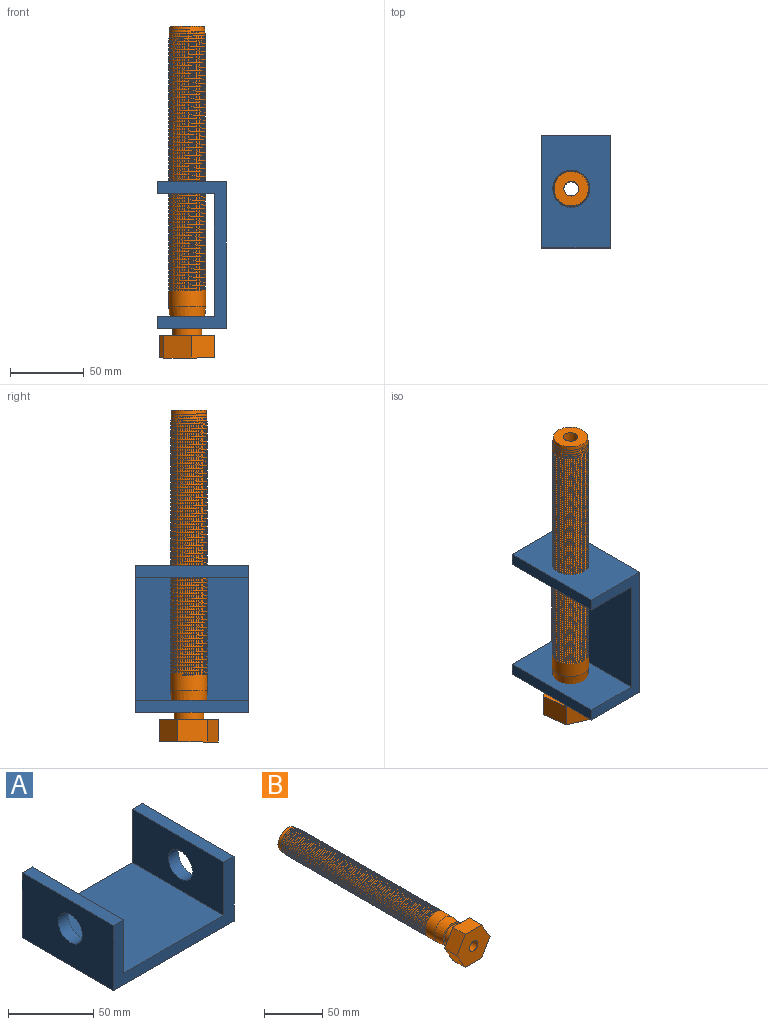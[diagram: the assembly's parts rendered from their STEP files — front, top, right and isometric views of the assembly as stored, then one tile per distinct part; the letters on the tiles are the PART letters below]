
ASSEMBLY  parts=2 mates=1
PART A: 12 faces, bbox 99.5x76x46.5 mm
  f0: plane 82.91x76mm, normal (0,0,1), area 6301.2mm2, adj f1,f7,f8,f9
  f1: plane 76x38.19mm, normal (1,0,0), area 2588mm2, adj f0,f2,f8,f9,f11
  f2: plane 76x8.3mm, normal (0,0,1), area 630.8mm2, adj f1,f3,f8,f9
  f3: plane 76x46.49mm, normal (-1,0,0), area 3218.8mm2, adj f2,f4,f8,f9,f11
  f4: plane 99.51x76mm, normal (0,0,-1), area 7562.8mm2, adj f3,f5,f8,f9
  f5: plane 76x46.49mm, normal (1,0,0), area 3218.8mm2, adj f4,f6,f8,f9,f10
  f6: plane 76x8.3mm, normal (0,0,1), area 630.8mm2, adj f5,f7,f8,f9
  f7: plane 76x38.19mm, normal (-1,0,0), area 2588mm2, adj f0,f6,f8,f9,f10
  f8: plane 99.51x46.49mm, normal (0,-1,0), area 1459.8mm2, adj f0,f1,f2,f3,f4,f5,f6,f7
  f9: plane 99.51x46.49mm, normal (0,1,0), area 1459.8mm2, adj f0,f1,f2,f3,f4,f5,f6,f7
  f10: cylinder r=10mm len=20mm, axis (1,0,0), area 521.5mm2, adj f5,f7
  f11: cylinder r=10mm len=20mm, axis (1,0,0), area 521.5mm2, adj f1,f3
PART B: 116 faces, bbox 40x225x34.6 mm
  f0: cylinder r=12.5mm len=25mm, axis (0,-1,0), area 899.1mm2, adj f93,f111,f112,f113,f114
  f1: cylinder r=12.5mm len=25mm, axis (0,-1,0), area 77.3mm2, adj f2,f94,f113,f114
  f2: cylinder r=12.5mm len=25mm, axis (0,-1,0), area 77.3mm2, adj f1,f3,f113,f114
  f3: cylinder r=12.5mm len=25mm, axis (0,-1,0), area 77.2mm2, adj f2,f4,f113,f114
  f4: cylinder r=12.5mm len=25mm, axis (0,-1,0), area 77.3mm2, adj f3,f5,f113,f114
  f5: cylinder r=12.5mm len=25mm, axis (0,-1,0), area 77.3mm2, adj f4,f6,f113,f114
  f6: cylinder r=12.5mm len=25mm, axis (0,-1,0), area 77.3mm2, adj f5,f7,f113,f114
  f7: cylinder r=12.5mm len=25mm, axis (0,-1,0), area 77.3mm2, adj f6,f8,f113,f114
  f8: cylinder r=12.5mm len=25mm, axis (0,-1,0), area 77.3mm2, adj f7,f9,f113,f114
  f9: cylinder r=12.5mm len=25mm, axis (0,-1,0), area 77.3mm2, adj f8,f10,f113,f114
  f10: cylinder r=12.5mm len=25mm, axis (0,-1,0), area 77.4mm2, adj f9,f11,f113,f114
  f11: cylinder r=12.5mm len=25mm, axis (0,-1,0), area 77.4mm2, adj f10,f12,f113,f114
  f12: cylinder r=12.5mm len=25mm, axis (0,-1,0), area 77.3mm2, adj f11,f13,f113,f114
  f13: cylinder r=12.5mm len=25mm, axis (0,-1,0), area 77.3mm2, adj f12,f14,f113,f114
  f14: cylinder r=12.5mm len=25mm, axis (0,-1,0), area 77.3mm2, adj f13,f15,f113,f114
  f15: cylinder r=12.5mm len=25mm, axis (0,-1,0), area 77.4mm2, adj f14,f16,f113,f114
  f16: cylinder r=12.5mm len=25mm, axis (0,-1,0), area 77.3mm2, adj f15,f17,f113,f114
  f17: cylinder r=12.5mm len=25mm, axis (0,-1,0), area 77.3mm2, adj f16,f18,f113,f114
  f18: cylinder r=12.5mm len=25mm, axis (0,-1,0), area 77.3mm2, adj f17,f19,f113,f114
  f19: cylinder r=12.5mm len=25mm, axis (0,-1,0), area 77.3mm2, adj f18,f20,f113,f114
  f20: cylinder r=12.5mm len=25mm, axis (0,-1,0), area 77.3mm2, adj f19,f21,f113,f114
  f21: cylinder r=12.5mm len=25mm, axis (0,-1,0), area 77.3mm2, adj f20,f22,f113,f114
  f22: cylinder r=12.5mm len=25mm, axis (0,-1,0), area 77.3mm2, adj f21,f23,f113,f114
  f23: cylinder r=12.5mm len=25mm, axis (0,-1,0), area 77.2mm2, adj f22,f24,f113,f114
  f24: cylinder r=12.5mm len=25mm, axis (0,-1,0), area 77.3mm2, adj f23,f25,f113,f114
  f25: cylinder r=12.5mm len=25mm, axis (0,-1,0), area 77.3mm2, adj f24,f26,f113,f114
  f26: cylinder r=12.5mm len=25mm, axis (0,-1,0), area 77.3mm2, adj f25,f27,f113,f114
  f27: cylinder r=12.5mm len=25mm, axis (0,-1,0), area 77.3mm2, adj f26,f28,f113,f114
  f28: cylinder r=12.5mm len=25mm, axis (0,-1,0), area 77.3mm2, adj f27,f29,f113,f114
  f29: cylinder r=12.5mm len=25mm, axis (0,-1,0), area 77.3mm2, adj f28,f30,f113,f114
  f30: cylinder r=12.5mm len=25mm, axis (0,-1,0), area 77.3mm2, adj f29,f31,f113,f114
  f31: cylinder r=12.5mm len=25mm, axis (0,-1,0), area 77.4mm2, adj f30,f32,f113,f114
  f32: cylinder r=12.5mm len=25mm, axis (0,-1,0), area 77.3mm2, adj f31,f33,f113,f114
  f33: cylinder r=12.5mm len=25mm, axis (0,-1,0), area 77.3mm2, adj f32,f34,f113,f114
  f34: cylinder r=12.5mm len=25mm, axis (0,-1,0), area 77.3mm2, adj f33,f35,f113,f114
  f35: cylinder r=12.5mm len=25mm, axis (0,-1,0), area 77.3mm2, adj f34,f36,f113,f114
  f36: cylinder r=12.5mm len=25mm, axis (0,-1,0), area 77.4mm2, adj f35,f37,f113,f114
  f37: cylinder r=12.5mm len=25mm, axis (0,-1,0), area 77.3mm2, adj f36,f38,f113,f114
  f38: cylinder r=12.5mm len=25mm, axis (0,-1,0), area 77.3mm2, adj f37,f39,f113,f114
  f39: cylinder r=12.5mm len=25mm, axis (0,-1,0), area 77.3mm2, adj f38,f40,f113,f114
  f40: cylinder r=12.5mm len=25mm, axis (0,-1,0), area 77.3mm2, adj f39,f41,f113,f114
  f41: cylinder r=12.5mm len=25mm, axis (0,-1,0), area 77.3mm2, adj f40,f42,f113,f114
  f42: cylinder r=12.5mm len=25mm, axis (0,-1,0), area 77.3mm2, adj f41,f43,f113,f114
  f43: cylinder r=12.5mm len=25mm, axis (0,-1,0), area 77.3mm2, adj f42,f44,f113,f114
  f44: cylinder r=12.5mm len=25mm, axis (0,-1,0), area 77.2mm2, adj f43,f45,f113,f114
  f45: cylinder r=12.5mm len=25mm, axis (0,-1,0), area 77.3mm2, adj f44,f46,f113,f114
  f46: cylinder r=12.5mm len=25mm, axis (0,-1,0), area 77.3mm2, adj f45,f47,f113,f114
  f47: cylinder r=12.5mm len=25mm, axis (0,-1,0), area 77.3mm2, adj f46,f48,f113,f114
  f48: cylinder r=12.5mm len=25mm, axis (0,-1,0), area 77.3mm2, adj f47,f49,f113,f114
  f49: cylinder r=12.5mm len=25mm, axis (0,-1,0), area 77.3mm2, adj f48,f50,f113,f114
  f50: cylinder r=12.5mm len=25mm, axis (0,-1,0), area 77.3mm2, adj f49,f51,f113,f114
  f51: cylinder r=12.5mm len=25mm, axis (0,-1,0), area 77.4mm2, adj f50,f52,f113,f114
  f52: cylinder r=12.5mm len=25mm, axis (0,-1,0), area 77.4mm2, adj f51,f53,f113,f114
  f53: cylinder r=12.5mm len=25mm, axis (0,-1,0), area 77.3mm2, adj f52,f54,f113,f114
  f54: cylinder r=12.5mm len=25mm, axis (0,-1,0), area 77.3mm2, adj f53,f55,f113,f114
  f55: cylinder r=12.5mm len=25mm, axis (0,-1,0), area 77.3mm2, adj f54,f56,f113,f114
  f56: cylinder r=12.5mm len=25mm, axis (0,-1,0), area 77.4mm2, adj f55,f57,f113,f114
  f57: cylinder r=12.5mm len=25mm, axis (0,-1,0), area 77.3mm2, adj f56,f58,f113,f114
  f58: cylinder r=12.5mm len=25mm, axis (0,-1,0), area 77.3mm2, adj f57,f59,f113,f114
  f59: cylinder r=12.5mm len=25mm, axis (0,-1,0), area 77.3mm2, adj f58,f60,f113,f114
  f60: cylinder r=12.5mm len=25mm, axis (0,-1,0), area 77.3mm2, adj f59,f61,f113,f114
  f61: cylinder r=12.5mm len=25mm, axis (0,-1,0), area 77.3mm2, adj f60,f62,f113,f114
  f62: cylinder r=12.5mm len=25mm, axis (0,-1,0), area 77.3mm2, adj f61,f63,f113,f114
  f63: cylinder r=12.5mm len=25mm, axis (0,-1,0), area 77.3mm2, adj f62,f64,f113,f114
  f64: cylinder r=12.5mm len=25mm, axis (0,-1,0), area 77.2mm2, adj f63,f65,f113,f114
  f65: cylinder r=12.5mm len=25mm, axis (0,-1,0), area 77.3mm2, adj f64,f66,f113,f114
  f66: cylinder r=12.5mm len=25mm, axis (0,-1,0), area 77.3mm2, adj f65,f67,f113,f114
  f67: cylinder r=12.5mm len=25mm, axis (0,-1,0), area 77.3mm2, adj f66,f68,f113,f114
  f68: cylinder r=12.5mm len=25mm, axis (0,-1,0), area 77.3mm2, adj f67,f69,f113,f114
  f69: cylinder r=12.5mm len=25mm, axis (0,-1,0), area 77.3mm2, adj f68,f70,f113,f114
  f70: cylinder r=12.5mm len=25mm, axis (0,-1,0), area 77.3mm2, adj f69,f71,f113,f114
  f71: cylinder r=12.5mm len=25mm, axis (0,-1,0), area 77.3mm2, adj f70,f72,f113,f114
  f72: cylinder r=12.5mm len=25mm, axis (0,-1,0), area 77.4mm2, adj f71,f73,f113,f114
  f73: cylinder r=12.5mm len=25mm, axis (0,-1,0), area 77.3mm2, adj f72,f74,f113,f114
  f74: cylinder r=12.5mm len=25mm, axis (0,-1,0), area 77.3mm2, adj f73,f75,f113,f114
  f75: cylinder r=12.5mm len=25mm, axis (0,-1,0), area 77.3mm2, adj f74,f76,f113,f114
  f76: cylinder r=12.5mm len=25mm, axis (0,-1,0), area 77.4mm2, adj f75,f77,f113,f114
  f77: cylinder r=12.5mm len=25mm, axis (0,-1,0), area 77.4mm2, adj f76,f78,f113,f114
  f78: cylinder r=12.5mm len=25mm, axis (0,-1,0), area 77.3mm2, adj f77,f79,f113,f114
  f79: cylinder r=12.5mm len=25mm, axis (0,-1,0), area 77.3mm2, adj f78,f80,f113,f114
  f80: cylinder r=12.5mm len=25mm, axis (0,-1,0), area 77.3mm2, adj f79,f81,f113,f114
  f81: cylinder r=12.5mm len=25mm, axis (0,-1,0), area 77.3mm2, adj f80,f82,f113,f114
  f82: cylinder r=12.5mm len=25mm, axis (0,-1,0), area 77.3mm2, adj f81,f83,f113,f114
  f83: cylinder r=12.5mm len=25mm, axis (0,-1,0), area 77.3mm2, adj f82,f84,f113,f114
  f84: cylinder r=12.5mm len=25mm, axis (0,-1,0), area 77.2mm2, adj f83,f85,f113,f114
  f85: cylinder r=12.5mm len=25mm, axis (0,-1,0), area 77.2mm2, adj f84,f86,f113,f114
  f86: cylinder r=12.5mm len=25mm, axis (0,-1,0), area 77.3mm2, adj f85,f87,f113,f114
  f87: cylinder r=12.5mm len=25mm, axis (0,-1,0), area 77.3mm2, adj f86,f88,f113,f114
  f88: cylinder r=12.5mm len=25mm, axis (0,-1,0), area 77.3mm2, adj f87,f89,f113,f114
  f89: cylinder r=12.5mm len=25mm, axis (0,-1,0), area 77.3mm2, adj f88,f90,f113,f114
  f90: cylinder r=12.5mm len=25mm, axis (0,-1,0), area 77.3mm2, adj f89,f91,f113,f114
  f91: cylinder r=12.5mm len=25mm, axis (0,-1,0), area 77.3mm2, adj f90,f92,f113,f114
  f92: cylinder r=12.5mm len=25mm, axis (0,-1,0), area 77.4mm2, adj f91,f93,f113,f114
  f93: cylinder r=12.5mm len=25mm, axis (0,-1,0), area 77.4mm2, adj f0,f92,f113,f114
  f94: cylinder r=12.5mm len=24.17mm, axis (0,-1,0), area 21.2mm2, adj f1,f110,f113
  f95: plane 20x15mm, normal (0,0,1), area 300mm2, adj f96,f100,f101,f102
  f96: plane 17.32x15mm, normal (-0.87,0,0.5), area 300mm2, adj f95,f97,f101,f102
  f97: plane 17.32x15mm, normal (-0.87,0,-0.5), area 300mm2, adj f96,f98,f101,f102
  f98: plane 20x15mm, normal (0,0,-1), area 300mm2, adj f97,f99,f101,f102
  f99: plane 17.32x15mm, normal (0.87,0,-0.5), area 300mm2, adj f98,f100,f101,f102
  f100: plane 17.32x15mm, normal (0.87,0,0.5), area 300mm2, adj f95,f99,f101,f102
  f101: plane 40x34.64mm, normal (0,-1,0), area 960.7mm2, adj f95,f96,f97,f98,f99,f100,f115
  f102: plane 40x34.64mm, normal (0,1,0), area 725.1mm2, adj f95,f96,f97,f98,f99,f100,f103
  f103: cylinder r=10mm len=20mm, axis (0,-1,0), area 628.3mm2, adj f102,f105
  f104: plane 23.25x23.25mm, normal (0,1,0), area 346mm2, adj f106,f115
  f105: plane 23.25x23.25mm, normal (0,-1,0), area 110.4mm2, adj f103,f111
  f106: cone r=11.63mm half-angle=5deg, axis (0,-1,0), area 241.2mm2, adj f104,f107,f113,f114
  f107: cone r=11.63mm half-angle=5deg, axis (0,-1,0), area 121.5mm2, adj f106,f108,f113,f114
  f108: cone r=11.63mm half-angle=5deg, axis (0,-1,0), area 108.4mm2, adj f107,f109,f113,f114
  f109: cone r=11.63mm half-angle=5deg, axis (0,-1,0), area 94.8mm2, adj f108,f110,f113,f114
  f110: cone r=11.63mm half-angle=5deg, axis (0,-1,0), area 60.9mm2, adj f94,f109,f113,f114
  f111: cone r=12.5mm half-angle=5deg, axis (0,1,0), area 760.8mm2, adj f0,f105
  f112: plane 0.82x0.67mm, normal (0,0,-1), area 0.3mm2, adj f0,f113,f114
  f113: bspline ~177.6x29.55mm, area 5738.9mm2, adj f0,f1,f2,f3,f4,f5,f6,f7
  f114: bspline ~177.63x29.75mm, area 5748.1mm2, adj f0,f1,f2,f3,f4,f5,f6,f7
  f115: cylinder r=5mm len=225mm, axis (0,-1,0), area 7068.6mm2, adj f101,f104
PLACE A rot(axis=(0.71,0,-0.71),180deg) t=(-4.9,-204.24,-84.12)mm fixed
PLACE B rot(axis=(0.14,0.7,0.7),164.4deg) t=(-31.38,-164.24,-138.88)mm
MATE revolute B.f0 <-> A.f10  axis (0,0,-1) through (-31.38,-164.24,-133.88)mm
